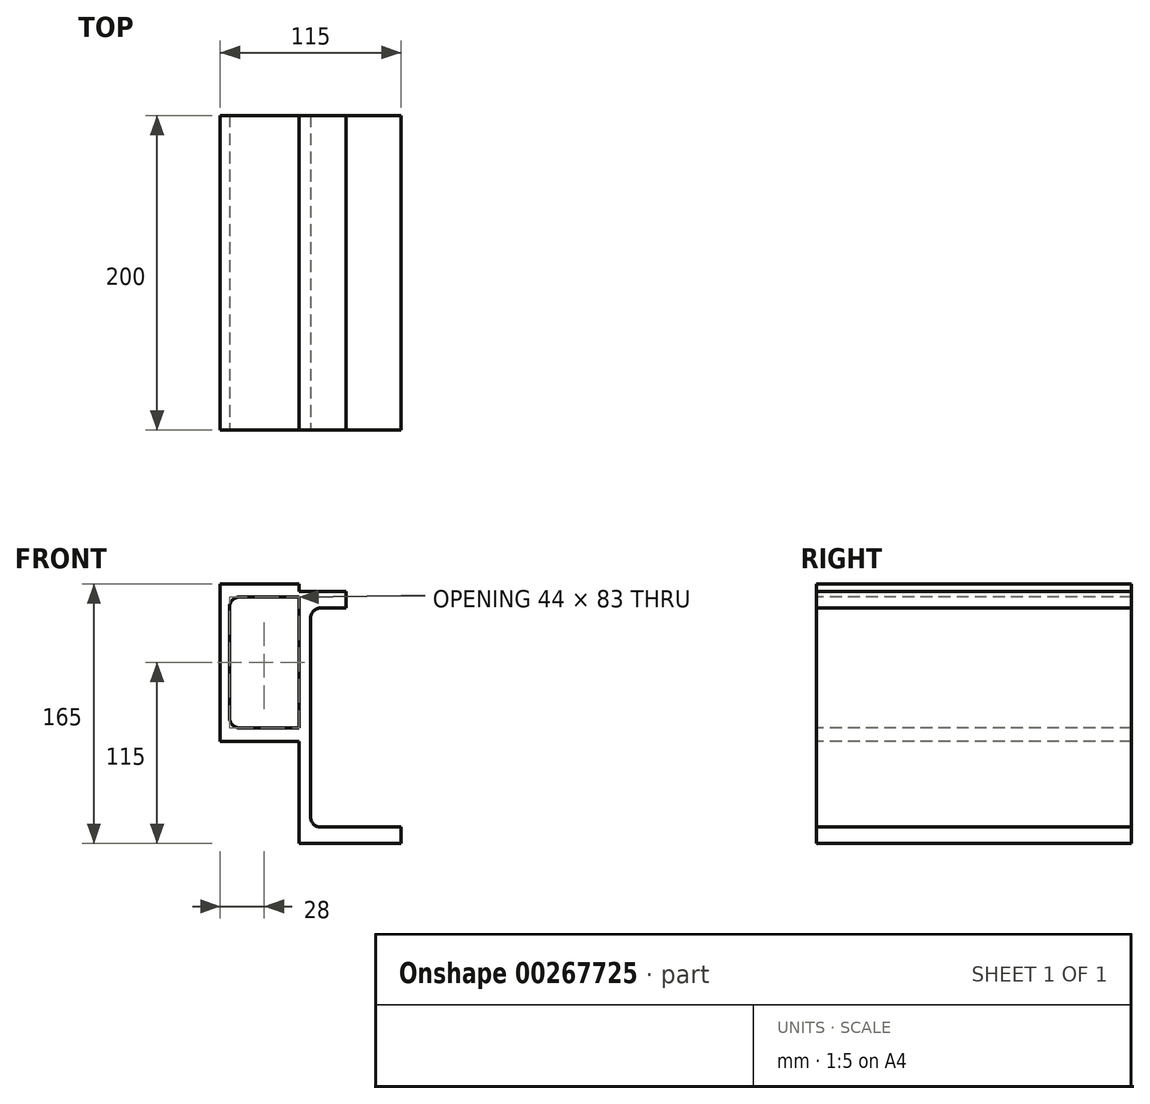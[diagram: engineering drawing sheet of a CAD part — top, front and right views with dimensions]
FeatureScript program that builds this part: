
annotation { "Feature Type Name" : "Feature", "Feature Type Description" : "" }
export const myFeature = defineFeature(function(context is Context, id is Id, definition is map)
    precondition{}
    {
        {
            var Q0;
            Q0=qCreatedBy(makeId("Front.planeOp"),FACE);
            var sketch = newSketch(context, id + "F0", { "sketchPlane" : qUnion([Q0])});
            skLineSegment(sketch, "E0.bottom", {"start": v(-2.5, 80) * mm, "end": v(-32.5, 80) * mm});
            skLineSegment(sketch, "E0.top", {"start": v(32.5, -80) * mm, "end": v(-32.5, -80) * mm});
            skLineSegment(sketch, "E0.right", {"start": v(-32.5, 80) * mm, "end": v(-32.5, -80) * mm});
            skPoint(sketch, "E0.middle", {"position": v(0, 0) * mm});
            skLineSegment(sketch, "E1.0", {"start": v(-2.5, 69.5) * mm, "end": v(-19, 69.5) * mm});
            skLineSegment(sketch, "E2.0", {"start": v(32.5, -69.5) * mm, "end": v(-19, -69.5) * mm});
            skLineSegment(sketch, "E3.0", {"start": v(-25, 63.5) * mm, "end": v(-25, -63.5) * mm});
            skArc(sketch, "E4.filletArc", {"start": v(-19, 69.5) * mm, "mid": v(-23.24, 67.74) * mm, "end": v(-25, 63.5) * mm});
            skArc(sketch, "E5.filletArc", {"start": v(-25, -63.5) * mm, "mid": v(-23.24, -67.74) * mm, "end": v(-19, -69.5) * mm});
            skLineSegment(sketch, "E6.trimOffspring", {"start": v(32.5, -69.5) * mm, "end": v(32.5, -80) * mm});
            skLineSegment(sketch, "E7.bottom", {"start": v(-32.5, -80) * mm, "end": v(-25, -80) * mm});
            skLineSegment(sketch, "E8.bottom", {"start": v(-32.5, 80) * mm, "end": v(-25, 80) * mm});
            skLineSegment(sketch, "E8.top", {"start": v(-32.5, 140) * mm, "end": v(-25, 140) * mm});
            skLineSegment(sketch, "E8.left", {"start": v(-32.5, 80) * mm, "end": v(-32.5, 140) * mm});
            skLineSegment(sketch, "E8.right", {"start": v(-25, 80) * mm, "end": v(-25, 140) * mm});
            skLineSegment(sketch, "E9", {"start": v(-2.5, 80) * mm, "end": v(-2.5, 69.5) * mm});
            skLineSegment(sketch, "E10.bottom", {"start": v(-32.5, 85) * mm, "end": v(-82.5, 85) * mm});
            skLineSegment(sketch, "E10.top", {"start": v(-32.5, -15) * mm, "end": v(-82.5, -15) * mm});
            skLineSegment(sketch, "E10.left", {"start": v(-32.5, 85) * mm, "end": v(-32.5, -15) * mm});
            skLineSegment(sketch, "E10.right", {"start": v(-82.5, 85) * mm, "end": v(-82.5, -15) * mm});
            skLineSegment(sketch, "E11.0", {"start": v(-32.5, -6.5) * mm, "end": v(-70.5, -6.5) * mm});
            skLineSegment(sketch, "E11.2", {"start": v(-32.5, 76.5) * mm, "end": v(-70.5, 76.5) * mm});
            skLineSegment(sketch, "E12.0", {"start": v(-76.5, 70.5) * mm, "end": v(-76.5, -0.5) * mm});
            skArc(sketch, "E13.filletArc", {"start": v(-70.5, 76.5) * mm, "mid": v(-74.74, 74.74) * mm, "end": v(-76.5, 70.5) * mm});
            skArc(sketch, "E14.filletArc", {"start": v(-76.5, -0.5) * mm, "mid": v(-74.74, -4.74) * mm, "end": v(-70.5, -6.5) * mm});
            skSolve(sketch);
        }
        {
            var Q0;
            {var subQ3=sQuery(id+"F0.wireOp",EDGE,"E0.bottom");Q0=makeQuery(id+"F0.imprint","IMPRINT",FACE,{"disambiguationData":[TD([[makeQuery(id+"F0.imprint","IMPRINT",EDGE,{"derivedFrom":subQ3}),1.0]])]});}
            var Q1;
            Q1=makeQuery(id+"F0.imprint","IMPRINT",FACE,{"disambiguationData":[TD([[makeQuery(id+"F0.imprint","IMPRINT",EDGE,{"derivedFrom":sQuery(id+"F0.wireOp",EDGE,"E7.bottom")}),-1.0]])]});
            var Q2;
            Q2=makeQuery(id+"F0.imprint","IMPRINT",FACE,{"disambiguationData":[TD([[makeQuery(id+"F0.imprint","IMPRINT",EDGE,{"derivedFrom":sQuery(id+"F0.wireOp",EDGE,"E8.bottom")}),1.0]])]});
            var Q3;
            {var subQ3=sQuery(id+"F0.wireOp",EDGE,"E10.bottom");Q3=makeQuery(id+"F0.imprint","IMPRINT",FACE,{"disambiguationData":[TD([[makeQuery(id+"F0.imprint","IMPRINT",EDGE,{"derivedFrom":subQ3}),1.0]])]});}
            extrude(context, id + "F1", {"entities" : qUnion([Q0, Q1, Q2, Q3]), "oppositeDirection" : true, "depth" : 200 * mm});
        }
    });
